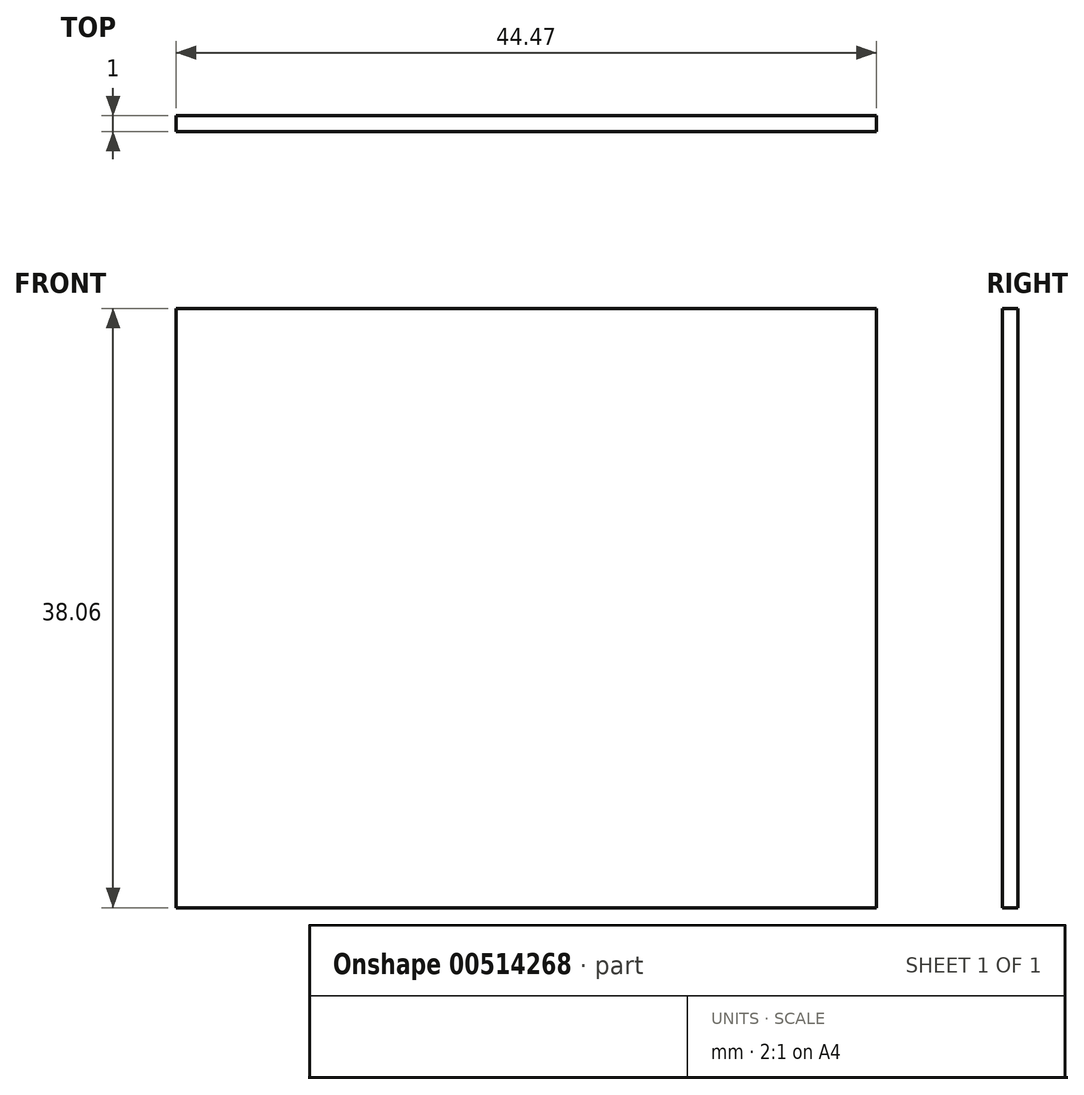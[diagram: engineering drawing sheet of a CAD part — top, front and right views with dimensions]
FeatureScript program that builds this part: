
annotation { "Feature Type Name" : "Feature", "Feature Type Description" : "" }
export const myFeature = defineFeature(function(context is Context, id is Id, definition is map)
    precondition{}
    {
        {
            var Q0;
            Q0=qCreatedBy(makeId("Front.planeOp"),FACE);
            var sketch = newSketch(context, id + "F0", { "sketchPlane" : qUnion([Q0])});
            skLineSegment(sketch, "E0.bottom", {"start": v(-22.29, 19.31) * mm, "end": v(22.18, 19.31) * mm});
            skLineSegment(sketch, "E0.top", {"start": v(-22.29, -18.75) * mm, "end": v(22.18, -18.75) * mm});
            skLineSegment(sketch, "E0.left", {"start": v(-22.29, 19.31) * mm, "end": v(-22.29, -18.75) * mm});
            skLineSegment(sketch, "E0.right", {"start": v(22.18, 19.31) * mm, "end": v(22.18, -18.75) * mm});
            skLineSegment(sketch, "E1", {"start": v(-22.29, 19.31) * mm, "end": v(22.18, -18.75) * mm});
            skSolve(sketch);
        }
        {
            var Q0;
            Q0=makeQuery(id+"F0.imprint","IMPRINT",FACE,{"disambiguationData":[TD([[makeQuery(id+"F0.imprint","IMPRINT",EDGE,{"derivedFrom":sQuery(id+"F0.wireOp",EDGE,"E0.bottom")}),-1.0]])]});
            var Q1;
            Q1=makeQuery(id+"F0.imprint","IMPRINT",FACE,{"disambiguationData":[TD([[makeQuery(id+"F0.imprint","IMPRINT",EDGE,{"derivedFrom":sQuery(id+"F0.wireOp",EDGE,"E0.top")}),1.0]])]});
            extrude(context, id + "F1", {"entities" : qUnion([Q0, Q1]), "depth" : 1 * mm});
        }
    });
